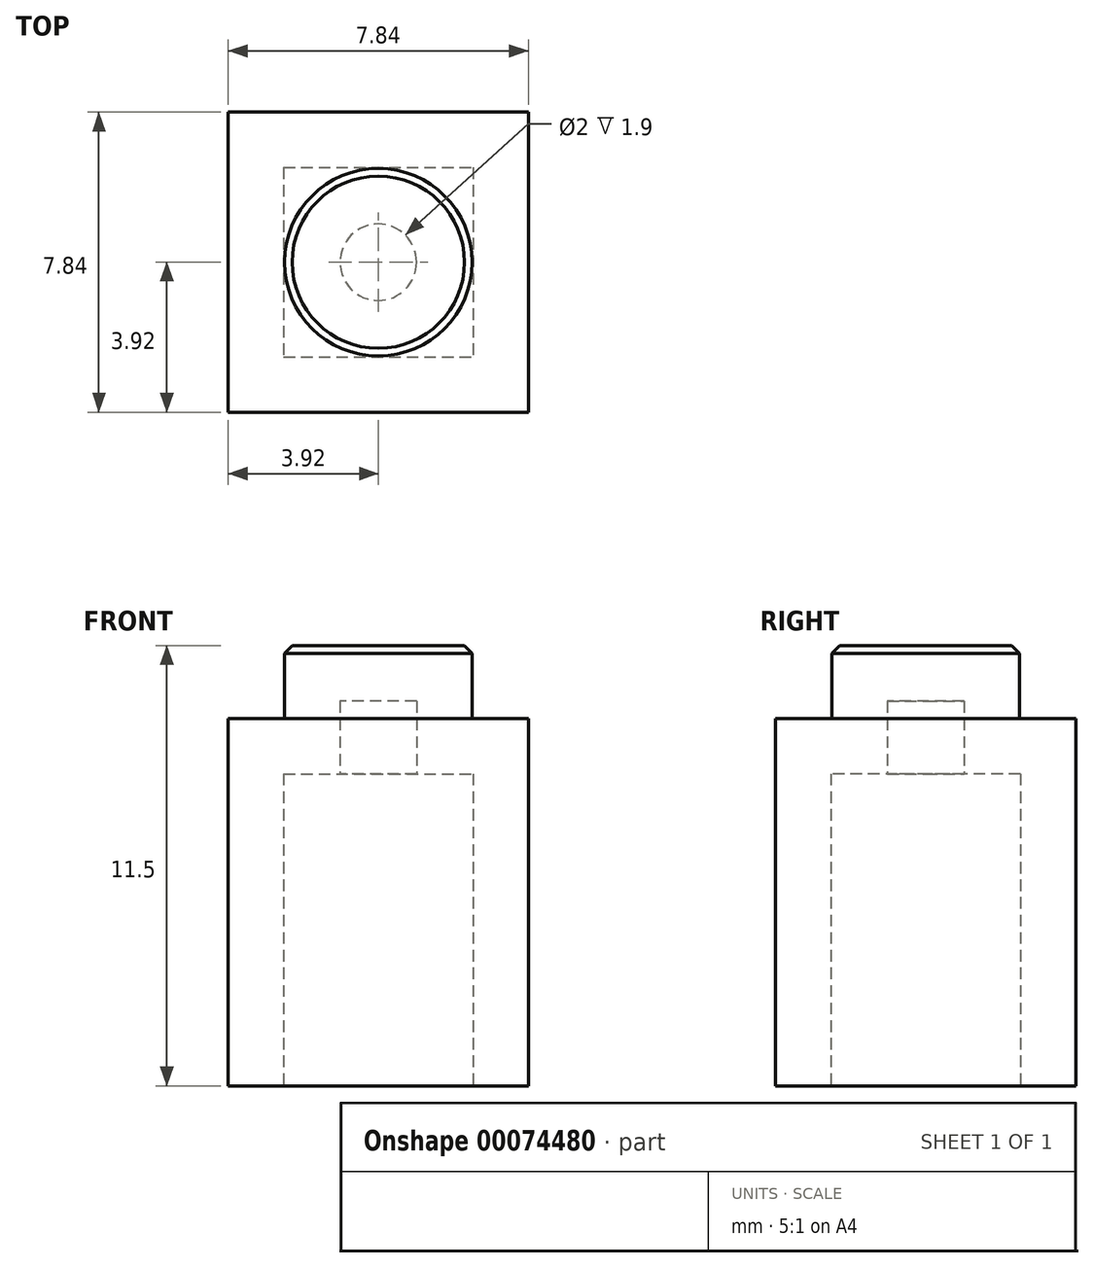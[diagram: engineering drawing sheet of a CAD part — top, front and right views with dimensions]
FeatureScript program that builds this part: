
annotation { "Feature Type Name" : "Feature", "Feature Type Description" : "" }
export const myFeature = defineFeature(function(context is Context, id is Id, definition is map)
    precondition{}
    {
        {
            var Q0;
            Q0=qCreatedBy(makeId("Top.planeOp"),FACE);
            var sketch = newSketch(context, id + "F0", { "sketchPlane" : qUnion([Q0])});
            skLineSegment(sketch, "E0.rect.bottom", {"start": v(-3.92, 3.92) * mm, "end": v(3.93, 3.92) * mm});
            skLineSegment(sketch, "E0.rect.top", {"start": v(-3.93, -3.92) * mm, "end": v(3.92, -3.92) * mm});
            skLineSegment(sketch, "E0.rect.left", {"start": v(-3.92, 3.92) * mm, "end": v(-3.93, -3.92) * mm});
            skLineSegment(sketch, "E0.rect.right", {"start": v(3.93, 3.92) * mm, "end": v(3.92, -3.92) * mm});
            skPoint(sketch, "E0.rect.middle", {"position": v(0, 0) * mm});
            skSolve(sketch);
        }
        {
            var Q0;
            Q0 = qSketchRegion(id + "F0", true);
            extrude(context, id + "F1", {"entities" : qUnion([Q0]), "depth" : 9.6 * mm});
        }
        {
            var Q0;
            Q0=makeQuery(id+"F1.opExtrude","CAP_FACE",FACE,{"disambiguationData":[OSD([sQuery(id+"F0.wireOp",EDGE,"E0.rect.bottom"),sQuery(id+"F0.wireOp",EDGE,"E0.rect.top"),sQuery(id+"F0.wireOp",EDGE,"E0.rect.left"),sQuery(id+"F0.wireOp",EDGE,"E0.rect.right")])],"isStart":false});
            var sketch = newSketch(context, id + "F2", { "sketchPlane" : qUnion([Q0])});
            skCircle(sketch, "E1", {"center": v(0, 0) * mm, "radius": 2.45 * mm});
            skSolve(sketch);
        }
        {
            var Q0;
            Q0 = qSketchRegion(id + "F2", true);
            extrude(context, id + "F3", {"entities" : qUnion([Q0]), "operationType" : NewBodyOperationType.ADD, "depth" : 1.9 * mm});
        }
        {
            var Q0;
            Q0=makeQuery(id+"F1.opExtrude","CAP_FACE",FACE,{"disambiguationData":[OSD([sQuery(id+"F0.wireOp",EDGE,"E0.rect.bottom"),sQuery(id+"F0.wireOp",EDGE,"E0.rect.top"),sQuery(id+"F0.wireOp",EDGE,"E0.rect.left"),sQuery(id+"F0.wireOp",EDGE,"E0.rect.right")])],"isStart":true});
            var Q1;
            Q1=makeQuery(id+"F1.opExtrude","SWEPT_BODY",BODY,{"disambiguationData":[OSD([sQuery(id+"F0.wireOp",EDGE,"E0.rect.bottom"),sQuery(id+"F0.wireOp",EDGE,"E0.rect.top"),sQuery(id+"F0.wireOp",EDGE,"E0.rect.left"),sQuery(id+"F0.wireOp",EDGE,"E0.rect.right")])]});
            shell(context, id + "F4", {"entities" : qUnion([Q0]), "parts" : qUnion([Q1]), "thickness" : 1.45 * mm});
        }
        {
            var Q0;
            Q0=makeQuery(id+"F3.opExtrude","CAP_EDGE",EDGE,{"disambiguationData":[OSD([sQuery(id+"F2.wireOp",EDGE,"E1")])],"isStart":false});
            chamfer(context, id + "F5", {"entities" : qUnion([Q0]), "width" : .2 * mm, "tangentPropagation" : true});
        }
    });
